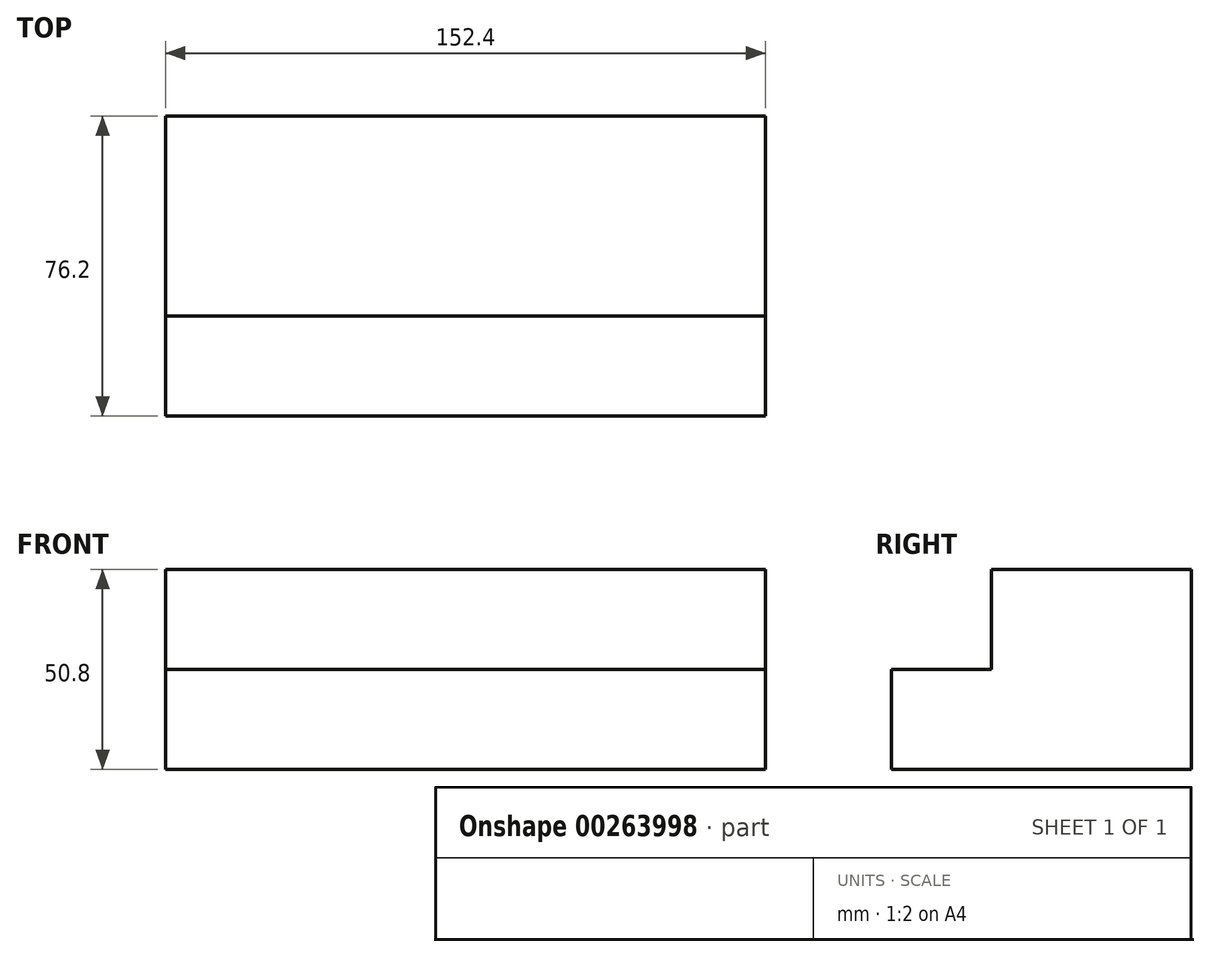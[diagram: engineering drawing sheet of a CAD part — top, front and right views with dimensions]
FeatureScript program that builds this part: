
annotation { "Feature Type Name" : "Feature", "Feature Type Description" : "" }
export const myFeature = defineFeature(function(context is Context, id is Id, definition is map)
    precondition{}
    {
        {
            var Q0;
            Q0=qCreatedBy(makeId("Right.planeOp"),FACE);
            var sketch = newSketch(context, id + "F0", { "sketchPlane" : qUnion([Q0])});
            skLineSegment(sketch, "E0", {"start": v(0, 0) * mm, "end": v(76.2, 0) * mm});
            skLineSegment(sketch, "E1", {"start": v(76.2, 0) * mm, "end": v(76.2, 50.8) * mm});
            skLineSegment(sketch, "E2", {"start": v(76.2, 50.8) * mm, "end": v(25.4, 50.8) * mm});
            skLineSegment(sketch, "E3", {"start": v(0, 0) * mm, "end": v(0, 25.4) * mm});
            skLineSegment(sketch, "E4", {"start": v(0, 25.4) * mm, "end": v(25.4, 25.4) * mm});
            skLineSegment(sketch, "E5", {"start": v(25.4, 25.4) * mm, "end": v(25.4, 50.8) * mm});
            skSolve(sketch);
        }
        {
            var Q0;
            Q0 = qSketchRegion(id + "F0", true);
            extrude(context, id + "F1", {"entities" : qUnion([Q0]), "depth" : 152.4 * mm});
        }
    });
